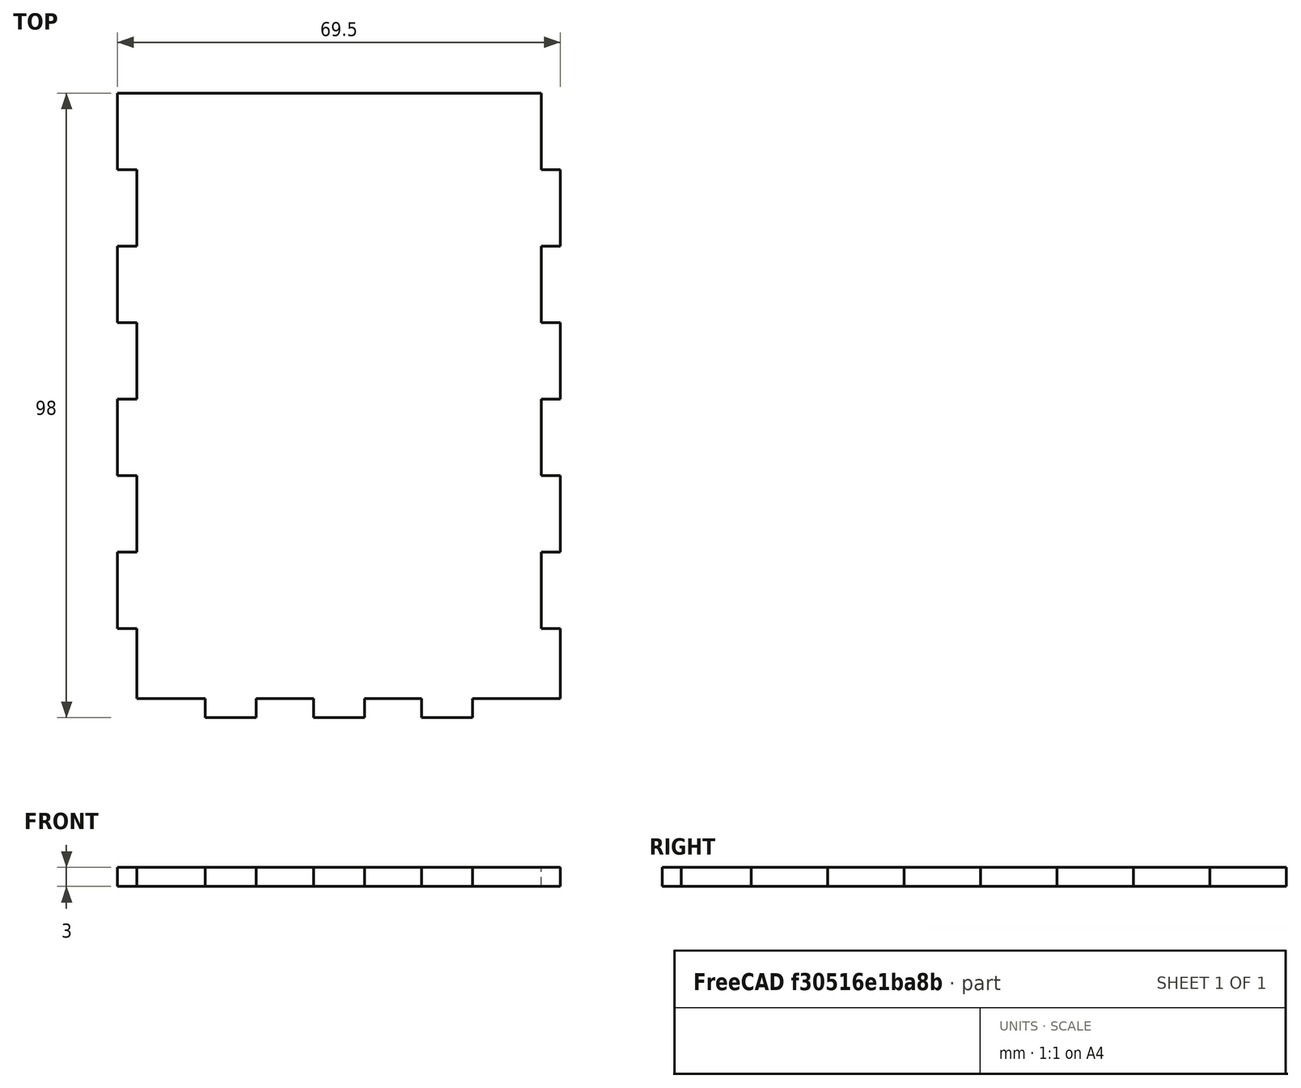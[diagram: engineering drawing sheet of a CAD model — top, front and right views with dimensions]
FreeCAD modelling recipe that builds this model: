
FCSTD DOCUMENT
Label: tea-light-side-1
objects: Sketcher::SketchObject×1, PartDesign::Pad×1
note: 3 computed .brp shape members not serialized (recipe doc carries the construction recipe); baked Part::Feature solids carry a one-line shape summary decoded from their .brp

FEATURE [Sketcher::SketchObject] Sketch
  sketch-geometry (44):
    g0: LineSegment StartX=34.75 StartY=-29 StartZ=0 EndX=21 EndY=-29 EndZ=0
    g1: LineSegment StartX=21 StartY=-29 StartZ=0 EndX=21 EndY=-32 EndZ=0
    g2: LineSegment StartX=21 StartY=-32 StartZ=0 EndX=13 EndY=-32 EndZ=0
    g3: LineSegment StartX=13 StartY=-32 StartZ=0 EndX=13 EndY=-29 EndZ=0
    g4: LineSegment StartX=13 StartY=-29 StartZ=0 EndX=4 EndY=-29 EndZ=0
    g5: LineSegment StartX=4 StartY=-29 StartZ=0 EndX=4 EndY=-32 EndZ=0
    g6: LineSegment StartX=4 StartY=-32 StartZ=0 EndX=-4 EndY=-32 EndZ=0
    g7: LineSegment StartX=-4 StartY=-32 StartZ=0 EndX=-4 EndY=-29 EndZ=0
    g8: LineSegment StartX=-4 StartY=-29 StartZ=0 EndX=-13 EndY=-29 EndZ=0
    g9: LineSegment StartX=-13 StartY=-29 StartZ=0 EndX=-13 EndY=-32 EndZ=0
    g10: LineSegment StartX=-13 StartY=-32 StartZ=0 EndX=-21 EndY=-32 EndZ=0
    g11: LineSegment StartX=-21 StartY=-32 StartZ=0 EndX=-21 EndY=-29 EndZ=0
    g12: LineSegment StartX=-21 StartY=-29 StartZ=0 EndX=-31.75 EndY=-29 EndZ=0
    g13: LineSegment StartX=-31.75 StartY=-29 StartZ=0 EndX=-31.75 EndY=-18 EndZ=0
    g14: LineSegment StartX=-31.75 StartY=-18 StartZ=0 EndX=-34.75 EndY=-18 EndZ=0
    g15: LineSegment StartX=-34.75 StartY=-18 StartZ=0 EndX=-34.75 EndY=-6 EndZ=0
    g16: LineSegment StartX=-34.75 StartY=-6 StartZ=0 EndX=-31.75 EndY=-6 EndZ=0
    g17: LineSegment StartX=-31.75 StartY=-6 StartZ=0 EndX=-31.75 EndY=6 EndZ=0
    g18: LineSegment StartX=-31.75 StartY=6 StartZ=0 EndX=-34.75 EndY=6 EndZ=0
    g19: LineSegment StartX=-34.75 StartY=6 StartZ=0 EndX=-34.75 EndY=18 EndZ=0
    g20: LineSegment StartX=-34.75 StartY=18 StartZ=0 EndX=-31.75 EndY=18 EndZ=0
    g21: LineSegment StartX=-31.75 StartY=18 StartZ=0 EndX=-31.75 EndY=30 EndZ=0
    g22: LineSegment StartX=-31.75 StartY=30 StartZ=0 EndX=-34.75 EndY=30 EndZ=0
    g23: LineSegment StartX=-34.75 StartY=30 StartZ=0 EndX=-34.75 EndY=42 EndZ=0
    g24: LineSegment StartX=-34.75 StartY=42 StartZ=0 EndX=-31.75 EndY=42 EndZ=0
    g25: LineSegment StartX=-31.75 StartY=42 StartZ=0 EndX=-31.75 EndY=54 EndZ=0
    g26: LineSegment StartX=-31.75 StartY=54 StartZ=0 EndX=-34.75 EndY=54 EndZ=0
    g27: LineSegment StartX=-34.75 StartY=54 StartZ=0 EndX=-34.75 EndY=66 EndZ=0
    g28: LineSegment StartX=-34.75 StartY=66 StartZ=0 EndX=31.75 EndY=66 EndZ=0
    g29: LineSegment StartX=31.75 StartY=66 StartZ=0 EndX=31.75 EndY=54 EndZ=0
    g30: LineSegment StartX=31.75 StartY=54 StartZ=0 EndX=34.75 EndY=54 EndZ=0
    g31: LineSegment StartX=34.75 StartY=54 StartZ=0 EndX=34.75 EndY=42 EndZ=0
    g32: LineSegment StartX=34.75 StartY=42 StartZ=0 EndX=31.75 EndY=42 EndZ=0
    g33: LineSegment StartX=31.75 StartY=42 StartZ=0 EndX=31.75 EndY=30 EndZ=0
    g34: LineSegment StartX=31.75 StartY=30 StartZ=0 EndX=34.75 EndY=30 EndZ=0
    g35: LineSegment StartX=34.75 StartY=30 StartZ=0 EndX=34.75 EndY=18 EndZ=0
    g36: LineSegment StartX=34.75 StartY=18 StartZ=0 EndX=31.75 EndY=18 EndZ=0
    g37: LineSegment StartX=31.75 StartY=18 StartZ=0 EndX=31.75 EndY=6 EndZ=0
    g38: LineSegment StartX=31.75 StartY=6 StartZ=0 EndX=34.75 EndY=6 EndZ=0
    g39: LineSegment StartX=34.75 StartY=6 StartZ=0 EndX=34.75 EndY=-6 EndZ=0
    g40: LineSegment StartX=34.75 StartY=-6 StartZ=0 EndX=31.75 EndY=-6 EndZ=0
    g41: LineSegment StartX=31.75 StartY=-6 StartZ=0 EndX=31.75 EndY=-18 EndZ=0
    g42: LineSegment StartX=31.75 StartY=-18 StartZ=0 EndX=34.75 EndY=-18 EndZ=0
    g43: LineSegment StartX=34.75 StartY=-18 StartZ=0 EndX=34.75 EndY=-29 EndZ=0
  constraints (132):
    c: Horizontal(g0)
    c: Coincident(g0,g1)
    c: Vertical(g1)
    c: Coincident(g1,g2)
    c: Horizontal(g2)
    c: Coincident(g2,g3)
    c: Vertical(g3)
    c: Coincident(g3,g4)
    c: Horizontal(g4)
    c: Coincident(g4,g5)
    c: Vertical(g5)
    c: Coincident(g5,g6)
    c: Coincident(g6,g7)
    c: Vertical(g7)
    c: Coincident(g7,g8)
    c: Horizontal(g8)
    c: Coincident(g8,g9)
    c: Vertical(g9)
    c: Coincident(g9,g10)
    c: Horizontal(g10)
    c: Coincident(g10,g11)
    c: Vertical(g11)
    c: Coincident(g11,g12)
    c: Horizontal(g12)
    c: Coincident(g12,g13)
    c: Vertical(g13)
    c: Coincident(g13,g14)
    c: Coincident(g14,g15)
    c: Vertical(g15)
    c: Coincident(g15,g16)
    c: Horizontal(g16)
    c: Coincident(g16,g17)
    c: Vertical(g17)
    c: Coincident(g17,g18)
    c: Coincident(g18,g19)
    c: Vertical(g19)
    c: Coincident(g19,g20)
    c: Coincident(g20,g21)
    c: Coincident(g21,g22)
    c: Horizontal(g22)
    c: Coincident(g22,g23)
    c: Vertical(g23)
    c: Coincident(g23,g24)
    c: Horizontal(g24)
    c: Coincident(g24,g25)
    c: Vertical(g25)
    c: Coincident(g25,g26)
    c: Horizontal(g26)
    c: Coincident(g26,g27)
    c: Vertical(g27)
    c: Coincident(g27,g28)
    c: Horizontal(g28)
    c: Coincident(g28,g29)
    c: Vertical(g29)
    c: Coincident(g29,g30)
    c: Horizontal(g30)
    c: Coincident(g30,g31)
    c: Vertical(g31)
    c: Coincident(g31,g32)
    c: Coincident(g32,g33)
    c: Vertical(g33)
    c: Coincident(g33,g34)
    c: Coincident(g34,g35)
    c: Coincident(g35,g36)
    c: Coincident(g36,g37)
    c: Vertical(g37)
    c: Coincident(g37,g38)
    c: Horizontal(g38)
    c: Coincident(g38,g39)
    c: Coincident(g39,g40)
    c: Horizontal(g40)
    c: Coincident(g40,g41)
    c: Coincident(g41,g42)
    c: Horizontal(g42)
    c: Coincident(g42,g43)
    c: Coincident(g43,g0)
    c: Horizontal(g14)
    c: Horizontal(g18)
    c: Horizontal(g20)
    c: Horizontal(g36)
    c: Horizontal(g32)
    c: Horizontal(g34)
    c: Vertical(g21)
    c: Vertical(g41)
    c: Vertical(g43)
    c: Vertical(g35)
    c: Vertical(g39)
    c: Symmetric(g25,g29,g-2)
    c: DistanceY(g7,g27) = 95
    c: DistanceX(g25,g29) = 63.5
    c: Equal(g11,g9)
    c: Equal(g9,g7)
    c: Equal(g7,g5)
    c: Equal(g5,g3)
    c: Equal(g3,g1)
    c: Equal(g38,g36)
    c: Equal(g36,g34)
    c: Equal(g34,g32)
    c: Equal(g32,g30)
    c: Equal(g30,g40)
    c: Equal(g40,g42)
    c: Equal(g1,g42)
    c: Equal(g14,g16)
    c: Equal(g16,g18)
    c: Equal(g18,g20)
    c: Equal(g20,g22)
    c: Equal(g22,g24)
    c: Equal(g24,g26)
    c: DistanceY(g1) = -3
    c: Equal(g14,g11)
    c: Equal(g10,g6)
    c: Equal(g6,g2)
    c: Equal(g8,g4)
    c: Symmetric(g6,g5,g-2)
    c: DistanceX(g10) = -8
    c: DistanceX(g4) = -9
    c: Equal(g13,g43)
    c: Equal(g15,g41)
    c: Equal(g17,g39)
    c: Equal(g19,g37)
    c: Equal(g35,g21)
    c: Equal(g23,g33)
    c: Equal(g25,g31)
    c: Equal(g27,g29)
    c: Symmetric(g38,g39,g-1)
    c: Equal(g23,g19)
    c: Equal(g19,g15)
    c: Equal(g17,g21)
    c: Equal(g21,g25)
    c: DistanceY(g37) = -12
    c: DistanceY(g35) = -12
    c: DistanceY(g27) = 12
FEATURE [PartDesign::Pad] Pad
  Length = 3
  Length2 = 100
  Sketch = -> Sketch
  Type = 0
